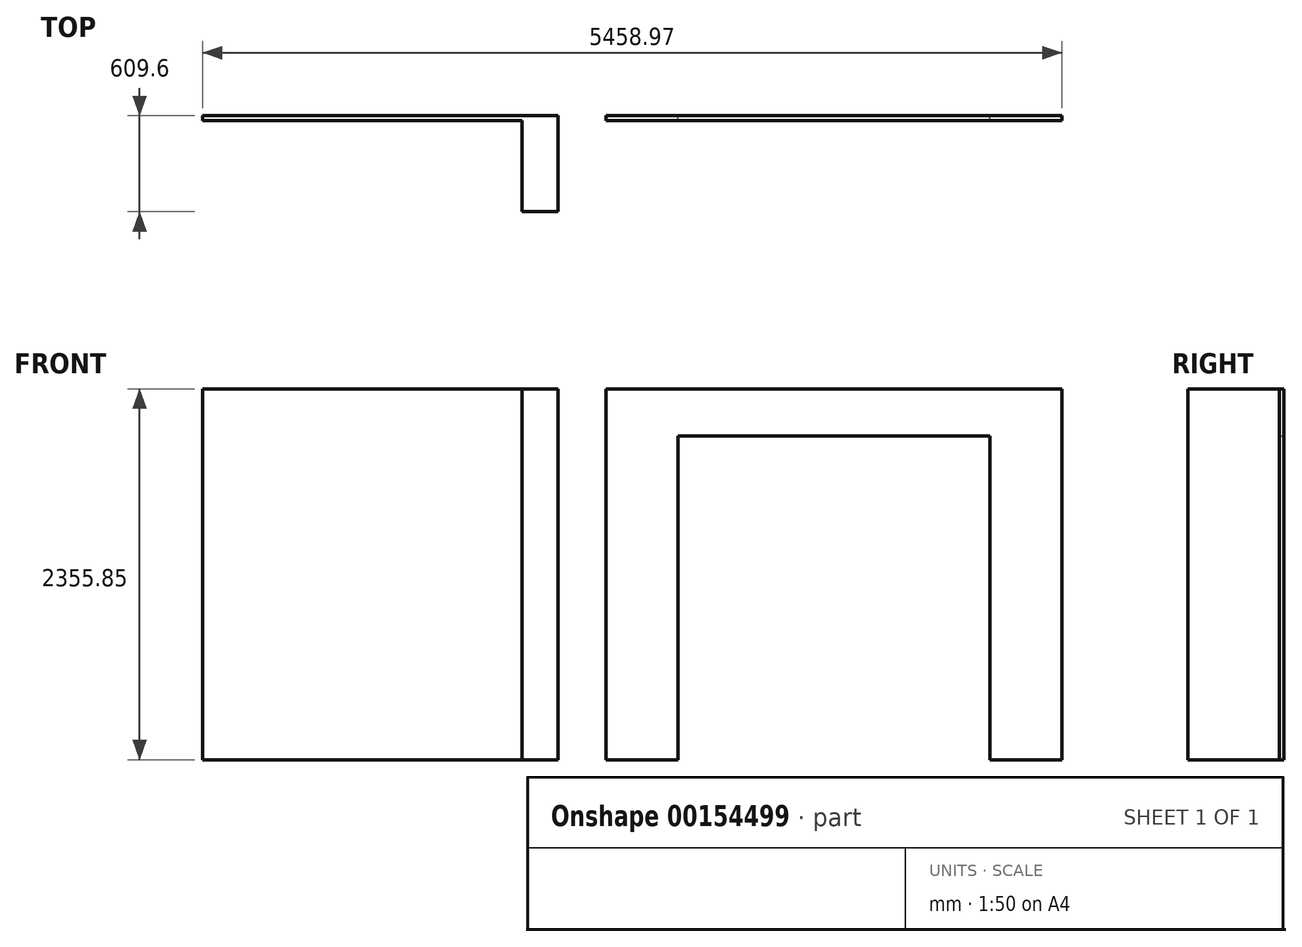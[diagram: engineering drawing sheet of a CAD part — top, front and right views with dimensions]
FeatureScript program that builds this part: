
annotation { "Feature Type Name" : "Feature", "Feature Type Description" : "" }
export const myFeature = defineFeature(function(context is Context, id is Id, definition is map)
    precondition{}
    {
        {
            var Q0;
            Q0=qCreatedBy(makeId("Front.planeOp"),FACE);
            var sketch = newSketch(context, id + "F0", { "sketchPlane" : qUnion([Q0])});
            skLineSegment(sketch, "E0.bottom", {"start": v(0, 0) * mm, "end": v(2895.6, 0) * mm});
            skLineSegment(sketch, "E0.top", {"start": v(0, 2355.85) * mm, "end": v(2895.6, 2355.85) * mm});
            skLineSegment(sketch, "E0.left", {"start": v(0, 0) * mm, "end": v(0, 2355.85) * mm});
            skLineSegment(sketch, "E0.right", {"start": v(2895.6, 0) * mm, "end": v(2895.6, 2355.85) * mm});
            skLineSegment(sketch, "E1.bottom", {"start": v(-533.4, 0) * mm, "end": v(-2563.37, 0) * mm});
            skLineSegment(sketch, "E1.top", {"start": v(-533.4, 2355.85) * mm, "end": v(-2563.37, 2355.85) * mm});
            skLineSegment(sketch, "E1.left", {"start": v(-533.4, 0) * mm, "end": v(-533.4, 2355.85) * mm});
            skLineSegment(sketch, "E1.right", {"start": v(-2563.37, 0) * mm, "end": v(-2563.37, 2355.85) * mm});
            skLineSegment(sketch, "E2", {"start": v(457.2, 0) * mm, "end": v(457.2, 2057.4) * mm});
            skLineSegment(sketch, "E3", {"start": v(457.2, 2057.4) * mm, "end": v(2438.4, 2057.4) * mm});
            skLineSegment(sketch, "E4", {"start": v(2438.4, 2057.4) * mm, "end": v(2438.4, 0) * mm});
            skLineSegment(sketch, "E5", {"start": v(457.2, 2057.4) * mm, "end": v(0, 2057.4) * mm, "construction": true});
            skLineSegment(sketch, "E6", {"start": v(2438.4, 2057.4) * mm, "end": v(2895.6, 2057.4) * mm, "construction": true});
            skLineSegment(sketch, "E7", {"start": v(-533.4, 2355.85) * mm, "end": v(-304.8, 2355.85) * mm});
            skLineSegment(sketch, "E8", {"start": v(-304.8, 2355.85) * mm, "end": v(-304.8, 0) * mm});
            skLineSegment(sketch, "E9", {"start": v(-304.8, 0) * mm, "end": v(-533.4, 0) * mm});
            skSolve(sketch);
        }
        {
            var Q0;
            Q0=makeQuery(id+"F0.imprint","IMPRINT",FACE,{"disambiguationData":[TD([[makeQuery(id+"F0.imprint","IMPRINT",EDGE,{"derivedFrom":sQuery(id+"F0.wireOp",EDGE,"E1.bottom")}),-1.0]])]});
            var Q1;
            Q1=makeQuery(id+"F0.imprint","IMPRINT",FACE,{"disambiguationData":[TD([[makeQuery(id+"F0.imprint","IMPRINT",EDGE,{"derivedFrom":sQuery(id+"F0.wireOp",EDGE,"E1.left")}),-1.0]])]});
            var Q2;
            Q2=makeQuery(id+"F0.imprint","IMPRINT",FACE,{"disambiguationData":[TD([[makeQuery(id+"F0.imprint","IMPRINT",EDGE,{"derivedFrom":sQuery(id+"F0.wireOp",EDGE,"E0.top")}),-1.0]])]});
            extrude(context, id + "F1", {"entities" : qUnion([Q0, Q1, Q2]), "depth" : 30.48 * mm});
        }
        {
            var Q0;
            Q0=makeQuery(id+"F0.imprint","IMPRINT",FACE,{"disambiguationData":[TD([[makeQuery(id+"F0.imprint","IMPRINT",EDGE,{"derivedFrom":sQuery(id+"F0.wireOp",EDGE,"E1.left")}),-1.0]])]});
            extrude(context, id + "F2", {"entities" : qUnion([Q0]), "operationType" : NewBodyOperationType.ADD, "depth" : 609.6 * mm});
        }
    });
